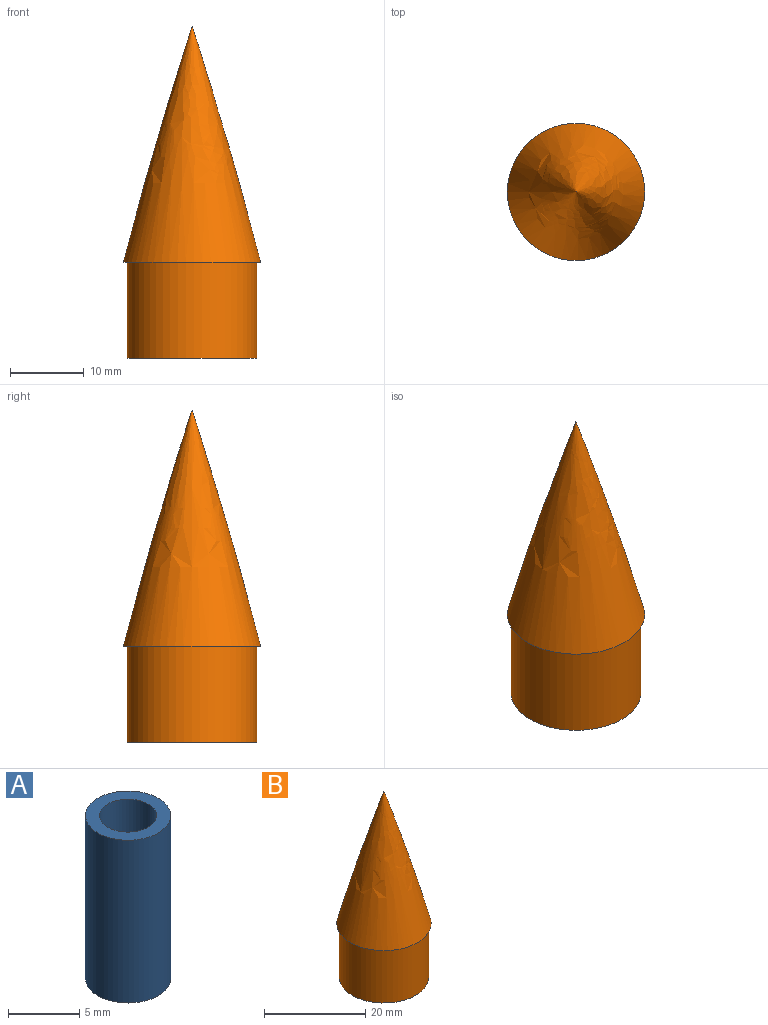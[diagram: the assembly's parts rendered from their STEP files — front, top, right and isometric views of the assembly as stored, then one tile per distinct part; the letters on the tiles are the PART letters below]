
ASSEMBLY  parts=2 mates=1
PART A: 4 faces, bbox 6x6x14 mm
  f0: cylinder r=2mm len=14mm, axis (0,0,-1), area 175.9mm2, adj f2,f3
  f1: cylinder r=3mm len=14mm, axis (0,0,-1), area 263.9mm2, adj f2,f3
  f2: plane 6x6mm, normal (0,0,1), area 15.7mm2, adj f0,f1
  f3: plane 6x6mm, normal (0,0,-1), area 15.7mm2, adj f0,f1
PART B: 7 faces, bbox 18.6x18.6x45 mm
  f0: plane 16.01x16.01mm, normal (0,0,1), area 10.2mm2, adj f1,f6
  f1: cylinder r=7.8mm len=15.6mm, axis (0,0,-1), area 686.1mm2, adj f0,f2
  f2: plane 17.6x17.6mm, normal (0,0,-1), area 52.2mm2, adj f1,f3
  f3: cylinder r=8.8mm len=17.6mm, axis (0,0,-1), area 718.8mm2, adj f2,f4
  f4: plane 18.6x18.6mm, normal (0,0,-1), area 28.4mm2, adj f3,f5
  f5: revolved ~31.99x18.6mm, area 1005.7mm2, adj f4
  f6: revolved ~27.7x16.01mm, area 746.3mm2, adj f0
PLACE A t=(5.43,0,25.01)mm
PLACE B at identity
MATE planar A.f0 <-> B.f1  axis (0,0,-1) through (5.43,0,25.01)mm
